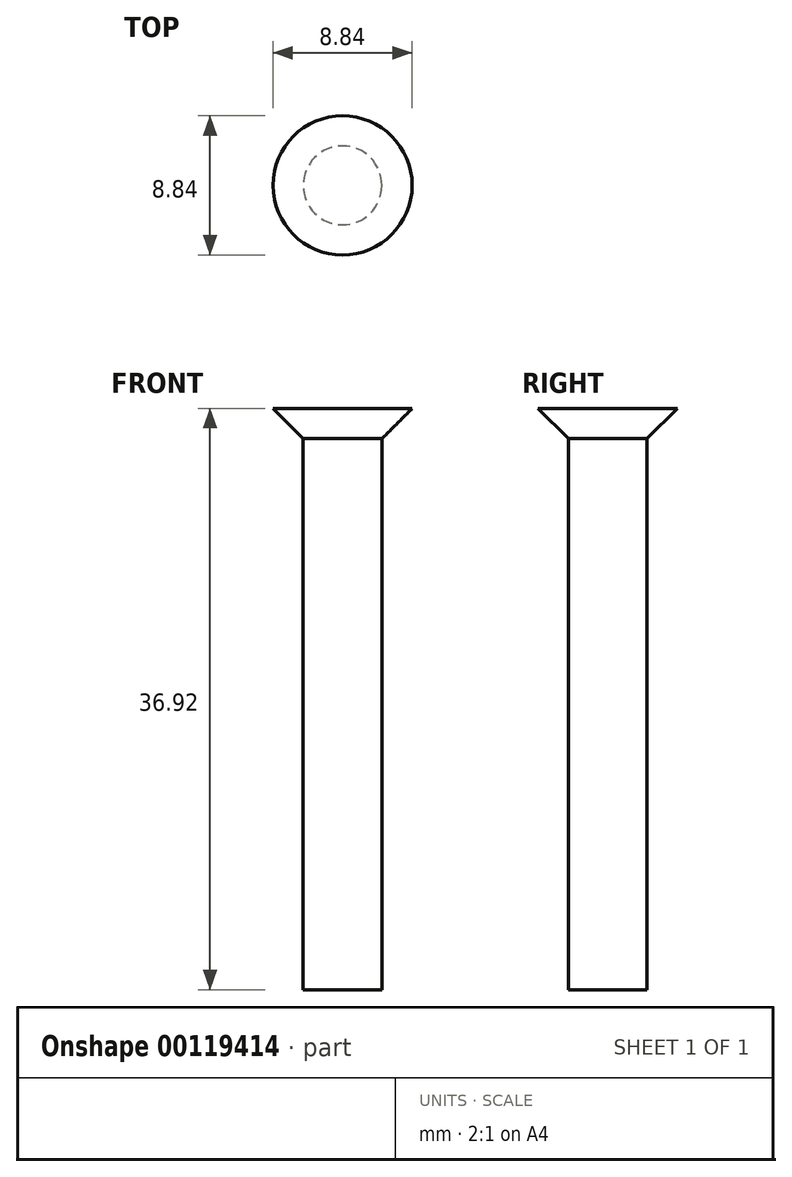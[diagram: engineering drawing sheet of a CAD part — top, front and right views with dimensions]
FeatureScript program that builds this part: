
annotation { "Feature Type Name" : "Feature", "Feature Type Description" : "" }
export const myFeature = defineFeature(function(context is Context, id is Id, definition is map)
    precondition{}
    {
        {
            var Q0;
            Q0=qCreatedBy(makeId("Front.planeOp"),FACE);
            var sketch = newSketch(context, id + "F0", { "sketchPlane" : qUnion([Q0])});
            skLineSegment(sketch, "E0", {"start": v(0, 28.51) * mm, "end": v(0, -10.66) * mm, "construction": true});
            skLineSegment(sketch, "E1.top", {"start": v(0, -14.55) * mm, "end": v(-2.5, -14.55) * mm});
            skLineSegment(sketch, "E1.right", {"start": v(-2.5, 20.45) * mm, "end": v(-2.5, -14.55) * mm});
            skLineSegment(sketch, "E2", {"start": v(-2.5, 20.45) * mm, "end": v(-4.42, 22.37) * mm});
            skLineSegment(sketch, "E3", {"start": v(-4.42, 22.37) * mm, "end": v(0, 22.37) * mm});
            skLineSegment(sketch, "E4", {"start": v(0, 22.37) * mm, "end": v(0, -14.55) * mm});
            skSolve(sketch);
        }
        {
            var Q0;
            Q0=qSketchRegion(id+"F0",true);
            var Q1;
            Q1=sQuery(id+"F0.wireOp",EDGE,"E0");
            revolve(context, id + "F1", {"entities" : qUnion([Q0]), "axis" : qUnion([Q1]), "revolveType" : RevolveType.FULL});
        }
    });
